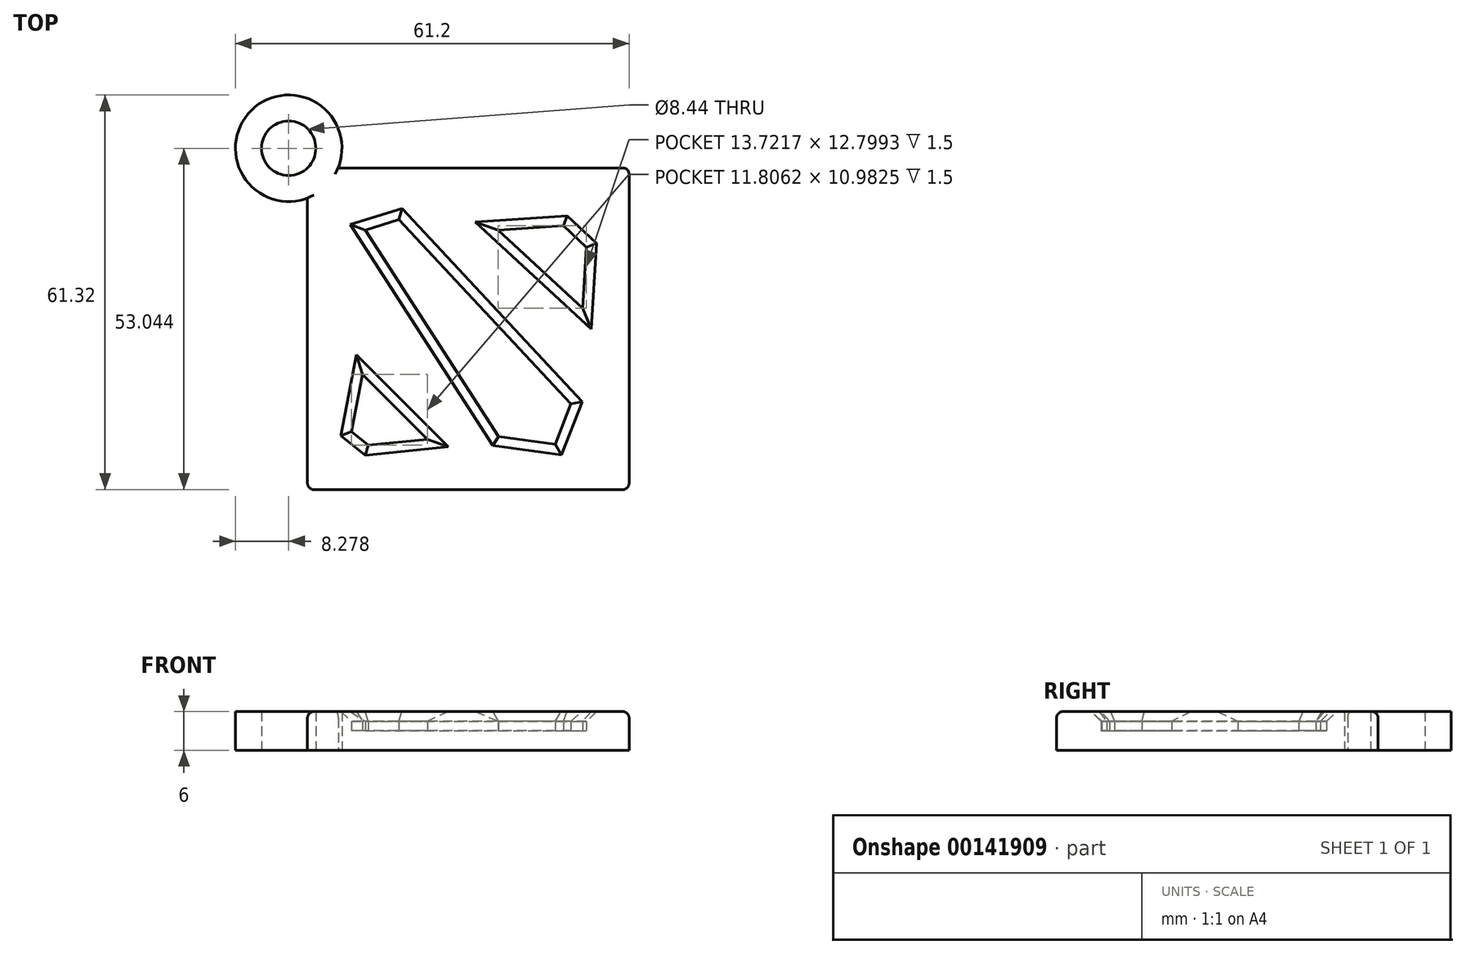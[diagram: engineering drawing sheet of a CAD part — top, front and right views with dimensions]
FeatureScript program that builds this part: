
annotation { "Feature Type Name" : "Feature", "Feature Type Description" : "" }
export const myFeature = defineFeature(function(context is Context, id is Id, definition is map)
    precondition{}
    {
        {
            var Q0;
            Q0=qCreatedBy(makeId("Top.planeOp"),FACE);
            var sketch = newSketch(context, id + "F0", { "sketchPlane" : qUnion([Q0])});
            skLineSegment(sketch, "E0.bottom", {"start": v(-13.9, 34.59) * mm, "end": v(31.33, 34.59) * mm});
            skLineSegment(sketch, "E0.top", {"start": v(-18.67, -15.41) * mm, "end": v(31.33, -15.41) * mm});
            skLineSegment(sketch, "E0.left", {"start": v(-18.67, 29.9) * mm, "end": v(-18.67, -15.41) * mm});
            skLineSegment(sketch, "E0.right", {"start": v(31.33, 34.59) * mm, "end": v(31.33, -15.41) * mm});
            skLineSegment(sketch, "E1", {"start": v(-9.69, 24.92) * mm, "end": v(11.02, -7.15) * mm});
            skLineSegment(sketch, "E2", {"start": v(22.28, -2.11) * mm, "end": v(-4.44, 26.54) * mm});
            skLineSegment(sketch, "E3", {"start": v(-4.44, 26.54) * mm, "end": v(-9.69, 24.92) * mm});
            skLineSegment(sketch, "E4", {"start": v(10.98, 24.9) * mm, "end": v(24.13, 12.8) * mm});
            skLineSegment(sketch, "E5", {"start": v(24.13, 12.8) * mm, "end": v(24.7, 22.25) * mm});
            skLineSegment(sketch, "E6", {"start": v(10.98, 24.9) * mm, "end": v(21.13, 25.6) * mm});
            skLineSegment(sketch, "E7", {"start": v(21.13, 25.6) * mm, "end": v(24.7, 22.25) * mm});
            skLineSegment(sketch, "E8", {"start": v(11.02, -7.15) * mm, "end": v(19.83, -8.36) * mm});
            skLineSegment(sketch, "E9", {"start": v(19.83, -8.36) * mm, "end": v(22.28, -2.11) * mm});
            skLineSegment(sketch, "E10", {"start": v(-0.06, -7.6) * mm, "end": v(-10.12, 2.46) * mm});
            skLineSegment(sketch, "E11", {"start": v(-10.12, 2.46) * mm, "end": v(-11.86, -6.41) * mm});
            skLineSegment(sketch, "E12", {"start": v(-0.06, -7.6) * mm, "end": v(-9.2, -8.52) * mm});
            skLineSegment(sketch, "E13", {"start": v(-9.2, -8.52) * mm, "end": v(-11.86, -6.41) * mm});
            skArc(sketch, "E14", {"start": v(-13.9, 34.59) * mm, "mid": v(-27.4, 43.53) * mm, "end": v(-18.67, 29.9) * mm});
            skCircle(sketch, "E15", {"center": v(-21.6, 37.63) * mm, "radius": 4.22 * mm});
            skPoint(sketch, "E16.orphan", {"position": v(-18.67, 34.59) * mm});
            skSolve(sketch);
        }
        {
            var Q0;
            Q0=makeQuery(id+"F0.imprint","IMPRINT",FACE,{"disambiguationData":[TD([[makeQuery(id+"F0.imprint","IMPRINT",EDGE,{"derivedFrom":sQuery(id+"F0.wireOp",EDGE,"E0.bottom")}),-1.0]])]});
            extrude(context, id + "F1", {"entities" : qUnion([Q0]), "depth" : 6 * mm});
        }
        {
            var Q0;
            Q0 = qSketchRegion(id + "F0", true);
            var Q1;
            Q1=makeQuery(id+"F0.imprint","IMPRINT",FACE,{"disambiguationData":[TD([[makeQuery(id+"F0.imprint","IMPRINT",EDGE,{"derivedFrom":sQuery(id+"F0.wireOp",EDGE,"E1")}),1.0]])]});
            var Q2;
            Q2=makeQuery(id+"F0.imprint","IMPRINT",FACE,{"disambiguationData":[TD([[makeQuery(id+"F0.imprint","IMPRINT",EDGE,{"derivedFrom":sQuery(id+"F0.wireOp",EDGE,"E4")}),1.0]])]});
            var Q3;
            Q3=makeQuery(id+"F0.imprint","IMPRINT",FACE,{"disambiguationData":[TD([[makeQuery(id+"F0.imprint","IMPRINT",EDGE,{"derivedFrom":sQuery(id+"F0.wireOp",EDGE,"E10")}),1.0]])]});
            extrude(context, id + "F2", {"entities" : qUnion([Q0, Q1, Q2, Q3]), "operationType" : NewBodyOperationType.ADD, "depth" : 3 * mm});
        }
        {
            var Q0;
            Q0=makeQuery(id+"F1.opExtrude","CAP_EDGE",EDGE,{"disambiguationData":[OSD([sQuery(id+"F0.wireOp",EDGE,"E2")])],"isStart":false});
            var Q1;
            Q1=makeQuery(id+"F1.opExtrude","CAP_EDGE",EDGE,{"disambiguationData":[OSD([sQuery(id+"F0.wireOp",EDGE,"E3")])],"isStart":false});
            var Q2;
            Q2=makeQuery(id+"F1.opExtrude","CAP_EDGE",EDGE,{"disambiguationData":[OSD([sQuery(id+"F0.wireOp",EDGE,"E1")])],"isStart":false});
            var Q3;
            Q3=makeQuery(id+"F1.opExtrude","CAP_EDGE",EDGE,{"disambiguationData":[OSD([sQuery(id+"F0.wireOp",EDGE,"E8")])],"isStart":false});
            var Q4;
            Q4=makeQuery(id+"F1.opExtrude","CAP_EDGE",EDGE,{"disambiguationData":[OSD([sQuery(id+"F0.wireOp",EDGE,"E9")])],"isStart":false});
            var Q5;
            Q5=makeQuery(id+"F1.opExtrude","CAP_EDGE",EDGE,{"disambiguationData":[OSD([sQuery(id+"F0.wireOp",EDGE,"E7")])],"isStart":false});
            var Q6;
            Q6=makeQuery(id+"F1.opExtrude","CAP_EDGE",EDGE,{"disambiguationData":[OSD([sQuery(id+"F0.wireOp",EDGE,"E6")])],"isStart":false});
            var Q7;
            Q7=makeQuery(id+"F1.opExtrude","CAP_EDGE",EDGE,{"disambiguationData":[OSD([sQuery(id+"F0.wireOp",EDGE,"E4")])],"isStart":false});
            var Q8;
            Q8=makeQuery(id+"F1.opExtrude","CAP_EDGE",EDGE,{"disambiguationData":[OSD([sQuery(id+"F0.wireOp",EDGE,"E5")])],"isStart":false});
            var Q9;
            Q9=makeQuery(id+"F1.opExtrude","CAP_EDGE",EDGE,{"disambiguationData":[OSD([sQuery(id+"F0.wireOp",EDGE,"E10")])],"isStart":false});
            var Q10;
            Q10=makeQuery(id+"F1.opExtrude","CAP_EDGE",EDGE,{"disambiguationData":[OSD([sQuery(id+"F0.wireOp",EDGE,"E11")])],"isStart":false});
            var Q11;
            Q11=makeQuery(id+"F1.opExtrude","CAP_EDGE",EDGE,{"disambiguationData":[OSD([sQuery(id+"F0.wireOp",EDGE,"E13")])],"isStart":false});
            var Q12;
            Q12=makeQuery(id+"F1.opExtrude","CAP_EDGE",EDGE,{"disambiguationData":[OSD([sQuery(id+"F0.wireOp",EDGE,"E12")])],"isStart":false});
            chamfer(context, id + "F3", {"entities" : qUnion([Q0, Q1, Q2, Q3, Q4, Q5, Q6, Q7, Q8, Q9, Q10, Q11, Q12]), "width" : 1.5 * mm, "tangentPropagation" : true});
        }
        {
            var Q0;
            Q0=makeQuery(id+"F1.opExtrude","CAP_EDGE",EDGE,{"disambiguationData":[OSD([sQuery(id+"F0.wireOp",EDGE,"E0.right")])],"isStart":false});
            var Q1;
            Q1=makeQuery(id+"F1.opExtrude","CAP_EDGE",EDGE,{"disambiguationData":[OSD([sQuery(id+"F0.wireOp",EDGE,"E0.top")])],"isStart":false});
            var Q2;
            Q2=makeQuery(id+"F1.opExtrude","CAP_EDGE",EDGE,{"disambiguationData":[OSD([sQuery(id+"F0.wireOp",EDGE,"E0.bottom")])],"isStart":false});
            var Q3;
            Q3=makeQuery(id+"F1.opExtrude","CAP_EDGE",EDGE,{"disambiguationData":[OSD([sQuery(id+"F0.wireOp",EDGE,"E0.left")])],"isStart":false});
            var Q4;
            Q4=makeQuery(id+"F1.opExtrude","SWEPT_EDGE",EDGE,{"disambiguationData":[OSD([sQuery(id+"F0.wireOp",EDGE,"E0.top"),sQuery(id+"F0.wireOp",EDGE,"E0.left")])]});
            var Q5;
            Q5=makeQuery(id+"F1.opExtrude","SWEPT_EDGE",EDGE,{"disambiguationData":[OSD([sQuery(id+"F0.wireOp",EDGE,"E0.top"),sQuery(id+"F0.wireOp",EDGE,"E0.right")])]});
            var Q6;
            Q6=makeQuery(id+"F1.opExtrude","SWEPT_EDGE",EDGE,{"disambiguationData":[OSD([sQuery(id+"F0.wireOp",EDGE,"E0.bottom"),sQuery(id+"F0.wireOp",EDGE,"E0.right")])]});
            fillet(context, id + "F4", {"entities" : qUnion([Q0, Q1, Q2, Q3, Q4, Q5, Q6]), "radius" : 1 * mm, "tangentPropagation" : true, "allowEdgeOverflow" : false});
        }
    });
